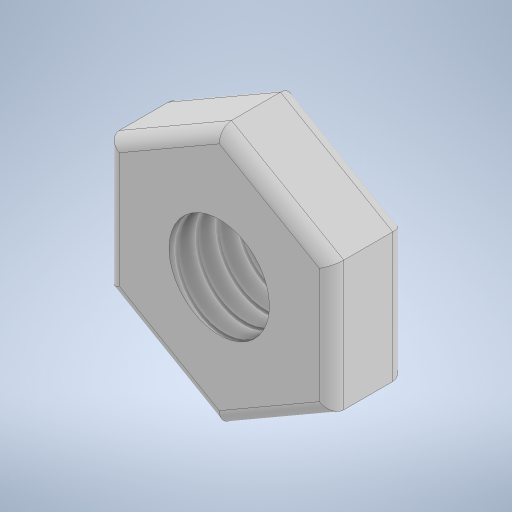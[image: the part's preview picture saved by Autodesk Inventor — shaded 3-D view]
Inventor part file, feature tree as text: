
AUTODESK INVENTOR PART (.ipt)
format: ipt  version: 2024 (Build 280153000, 153)  size: 257,024 bytes
history: native  units: in
note: dims shown in document units (in); Inventor stores cm internally (conversion verified against a paired STEP export)
features: extrude x1, thread x1, fillet x1, direct_edit x1, sketch x1, other x1
ambient origin geometry x8: Origin, YZ Plane, XZ Plane, XY Plane, X Axis, Y Axis, Z Axis, Center Point
bodies: Solid1 (feature_tree)
feature tree (6):
  extrude  "Extrusion1"  Depth=0.3937in
  thread  "Thread1"  [1 undecoded]
  fillet  "Fillet1"  Radius=0.0709in
  direct_edit  "Direct Edit1"
  sketch  "Sketch1"  dims[d0=0.0968in d1=0.1811in d2=0.25in d3=0.0709in d4=0.0in d5=0.3937in d6=0.0in d7=0.0118in d8=3.937in d9=0.3937in d10=0.3937in]
  other  "Scale1"
note: 1 required parameter value undecoded (feature->parameter linkage not recoverable at this tier; creation-order binding heuristic only, values carry confidence <= 0.55)
